# Revit family: QF_FISHER_1400
name_source: partatom
category: Specialty Equipment
revit_build: Autodesk Revit 2014 (Build: 20130308_1515(x64)
units: mm (PartAtom-declared; Revit-internal decimal feet)

## types (1)
- QF_FISHER_1400
    Cold Water Connection Height = 0"
    Cold Water Flow = 0 GPM
    Cold Water Maximum Pressure = 0.00 psi
    Cold Water Minimum Pressure = 0.00 psi
    Cold Water RI Height = 0"
    Cold Water Size = 0"
    Cold Water Temperature Recommended = 0 °F
    Depth = 10 1/8"
    Description = DROP-IN, WATER STATION
    Direct Waste Connection Height = 0"
    Direct Waste Flow = 0 GPM
    Direct Waste RI Height = 0"
    Direct Waste Size = 0"
    Fixture Finish = QF_Metal - Brass - Polished
    Foodservice Equipment Identifier = Yes
    Height = 9 1/2"
    Hot Water Connection Height = 0"
    Hot Water Consumption = 0 GPM
    Hot Water Flow = 0 GPM
    Hot Water Maximum Pressure = 0.00 psi
    Hot Water Minimum Pressure = 0.00 psi
    Hot Water RI Height = 0"
    Hot Water Size = 0"
    Hot Water Temperature = 0 °F
    Identify Quantity as Lot = Yes
    Indirect Waste Connection Height = 0"
    Indirect Waste Flow = 0 GPM
    Indirect Waste Size = 1"
    Length = 8 1/2"
    Lever Handle Off = No
    Manufacturer = FISHER
    Model = 1400
    Waste Water Discharge Temperature = 0 °F
    Weight in Pounds = 0
    Wrist Handle Off = Yes

## geometry (parser evidence)
native form markers: Blend x14, Sweep x11
no freeform markers — native parametric forms only
